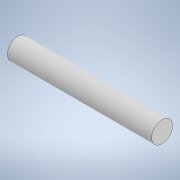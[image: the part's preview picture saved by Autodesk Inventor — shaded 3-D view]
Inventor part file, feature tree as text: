
AUTODESK INVENTOR PART (.ipt)
format: ipt  version: 2021 (Build 250183000, 183)  size: 90,112 bytes
history: native  units: mm
features: extrude x1, sketch x1
ambient origin geometry x8: Origin, YZ Plane, XZ Plane, XY Plane, X Axis, Y Axis, Z Axis, Center Point
bodies: Solid1 (feature_tree)
feature tree (2):
  extrude  "Extrusion1"  Depth=55.0mm TaperAngle=0.0deg
  sketch  "Sketch1"  dims[d0=8.0mm d1=55.0mm d2=0.0mm]
